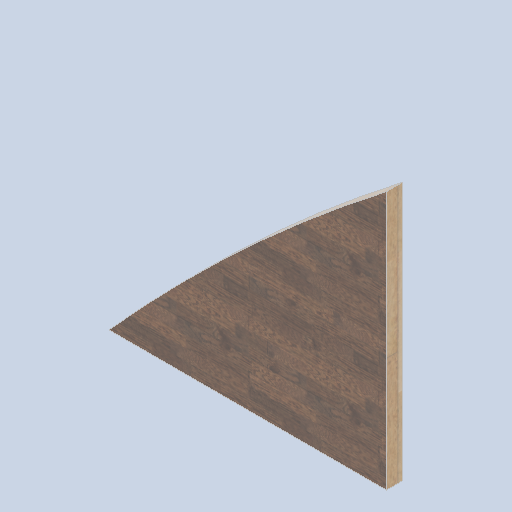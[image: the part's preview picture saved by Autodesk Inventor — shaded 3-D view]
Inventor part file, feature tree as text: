
AUTODESK INVENTOR PART (.ipt)
format: ipt  version: 2024.2 (Build 282272000, 272)  size: 172,032 bytes
history: native  units: in
note: dims shown in document units (in); Inventor stores cm internally (conversion verified against a paired STEP export)
features: other x3, sketch x1
ambient origin geometry x8: Origin, YZ Plane, XZ Plane, XY Plane, X Axis, Y Axis, Z Axis, Center Point
bodies: Solid1 (feature_tree)
feature tree (4):
  other  "front_wall_block01.ipt"
  other  "Solid1::front_wall_block01.ipt"
  other  "TaggingFeature1"
  sketch  "Sketch1"  dims[d0=0.3937in]
